# Revit family: Elkay_Drinking-Water_Bottle-Filling-Stations_EZ_Onwall_St2_Asiapac
name_source: partatom
category: Plumbing Fixtures
units: mm (PartAtom-declared; Revit-internal decimal feet)

## family parameters
Always vertical = Yes
Cut with Voids When Loaded = No
Part Type = Normal
Room Calculation Point = No
Round Connector Dimension = Use Diameter
Shared = No
Work Plane-Based = No

## types (17) — shared parameters
Activation by = Electronic Bottle Filler Sensor With Electronic Front And Side Bubbler Pushbar
Base With out Grill = Yes
Basin3 = Yes
Chilling Capacity = 8.0 GPH
Dimensions (L x W x H) = 36 3/4 inch x 19 inch x 39 1/16 inch
Full Load Amps = 3
GreenSpec Logo = Yes
Installation Location = Indoor
Manufacturer = Elkay
Mounting Type = Wall Mount (On Wall)
Number of Stations = 2
Push Button = Yes
Rated Watts = 370
Version = 1.0.0.0

## per-type parameters (varying)
| type | Approx. Shipping Weight | Bubbler Style | Elkay Rectangle size Bottom Basin Elkay Logo | Finish | Finish_1 | Flexiguard Bubbler | GreenSpec & Sensor Logo | Power | Special Features | Vandal Resistant |
| LZSTL8WSL2K | 106 lbs | Flexi-Guard ® Safety Bubbler | Yes | Light Gray Granite | Light Gray Granite | Yes | Yes | 220V/50Hz | Hands Free, Visual Filter Monitor, Filtered, Green Ticker™, Laminar Flow, Antimicrobial, Real Drain | No |
| LZSTL8WSL3K | 106 lbs | Flexi-Guard ® Safety Bubbler | Yes | Light Gray Granite | Light Gray Granite | Yes | Yes | 220V/60Hz | Hands Free, Visual Filter Monitor, Filtered, Green Ticker™, Laminar Flow, Antimicrobial, Real Drain | Yes |
| LZSTL8WSS2K | 106 lbs | Flexi-Guard ® Safety Bubbler | Yes | Stainless Steel | 304 Stainless Steel | Yes | Yes | 220V/50Hz | Hands Free, Visual Filter Monitor, Filtered, Green Ticker™, Laminar Flow, Antimicrobial, Real Drain | No |
| LZSTL8WSS3K | 106 lbs | Flexi-Guard ® Safety Bubbler | Yes | Stainless Steel | 304 Stainless Steel | Yes | Yes | 220V/60Hz | Hands Free, Visual Filter Monitor, Filtered, Green Ticker™, Laminar Flow, Antimicrobial, Real Drain | No |
| LZSTL8WSS3KSA | 106 lbs | Flexi-Guard ® Safety Bubbler | Yes | Stainless Steel | 304 Stainless Steel | Yes | Yes | 220V/60Hz | Hands Free, Visual Filter Monitor, Filtered, Green Ticker™, Laminar Flow, Antimicrobial, Real Drain | No |
| LZSTL8WSVRL2K | 94 lbs | Vandal Resistant | No | Light Gray Granite | Light Gray Granite | No | Yes | 220V/50Hz | Hands Free, Visual Filter Monitor, Filtered, Green Ticker™, Laminar Flow, Antimicrobial, Real Drain | Yes |
| LZSTL8WSVRL3K | 94 lbs | Vandal Resistant | No | Light Gray Granite | Light Gray Granite | No | Yes | 220V/60Hz | Hands Free, Visual Filter Monitor, Filtered, Green Ticker™, Laminar Flow, Antimicrobial, Real Drain | Yes |
| LZSTL8WSVRS2K | 94 lbs | Vandal Resistant | No | Stainless Steel | 304 Stainless Steel | No | Yes | 220V/50Hz | Hands Free, Visual Filter Monitor, Filtered, Green Ticker™, Laminar Flow, Antimicrobial, Real Drain | Yes |
| LZSTL8WSVRS3K | 94 lbs | Vandal Resistant | No | Stainless Steel | 304 Stainless Steel | No | Yes | 220V/60Hz | Hands Free, Visual Filter Monitor, Filtered, Green Ticker™, Laminar Flow, Antimicrobial, Real Drain | Yes |
| EZSTL8WSL2K | 89 lbs | Flexi-Guard ® Safety Bubbler | Yes | Light Gray Granite | Light Gray Granite | Yes | No | 220V/50Hz | Antimicrobial, Green Ticker™, Hands Free, Laminar Flow, Real Drain | No |
| EZSTL8WSL3K | 89 lbs | Flexi-Guard ® Safety Bubbler | Yes | Light Gray Granite | Light Gray Granite | Yes | No | 220V/60Hz | Antimicrobial, Green Ticker™, Hands Free, Laminar Flow, Real Drain | No |
| EZSTL8WSS2K | 89 lbs | Flexi-Guard ® Safety Bubbler | Yes | Stainless Steel | 304 Stainless Steel | Yes | No | 220V/50Hz | Antimicrobial, Green Ticker™, Hands Free, Laminar Flow, Real Drain | No |
| EZSTL8WSS3K | 89 lbs | Flexi-Guard ® Safety Bubbler | Yes | Stainless Steel | 304 Stainless Steel | Yes | No | 220V/60Hz | Antimicrobial, Green Ticker™, Hands Free, Laminar Flow, Real Drain | No |
| EZSTL8WSVRL2K | 91 lbs | Vandal Resistant | No | Light Gray Granite | Light Gray Granite | No | No | 220V/50Hz | Antimicrobial, Green Ticker™, Hands Free, Laminar Flow, Real Drain | Yes |
| EZSTL8WSVRL3K | 91 lbs | Vandal Resistant | No | Light Gray Granite | Light Gray Granite | No | No | 220V/60Hz | Antimicrobial, Green Ticker™, Hands Free, Laminar Flow, Real Drain | Yes |
| EZSTL8WSVRS2K | 91 lbs | Vandal Resistant | No | Stainless Steel | 304 Stainless Steel | No | No | 220V/50Hz | Antimicrobial, Green Ticker™, Hands Free, Laminar Flow, Real Drain | Yes |
| EZSTL8WSVRS3K | 91 lbs | Vandal Resistant | No | Stainless Steel | 304 Stainless Steel | No | No | 220V/60Hz | Antimicrobial, Green Ticker™, Hands Free, Laminar Flow, Real Drain | Yes |

note: column(s) folded — value = type name in every type: Model

## geometry (parser evidence)
native form markers: Sweep x44
no freeform markers — native parametric forms only
